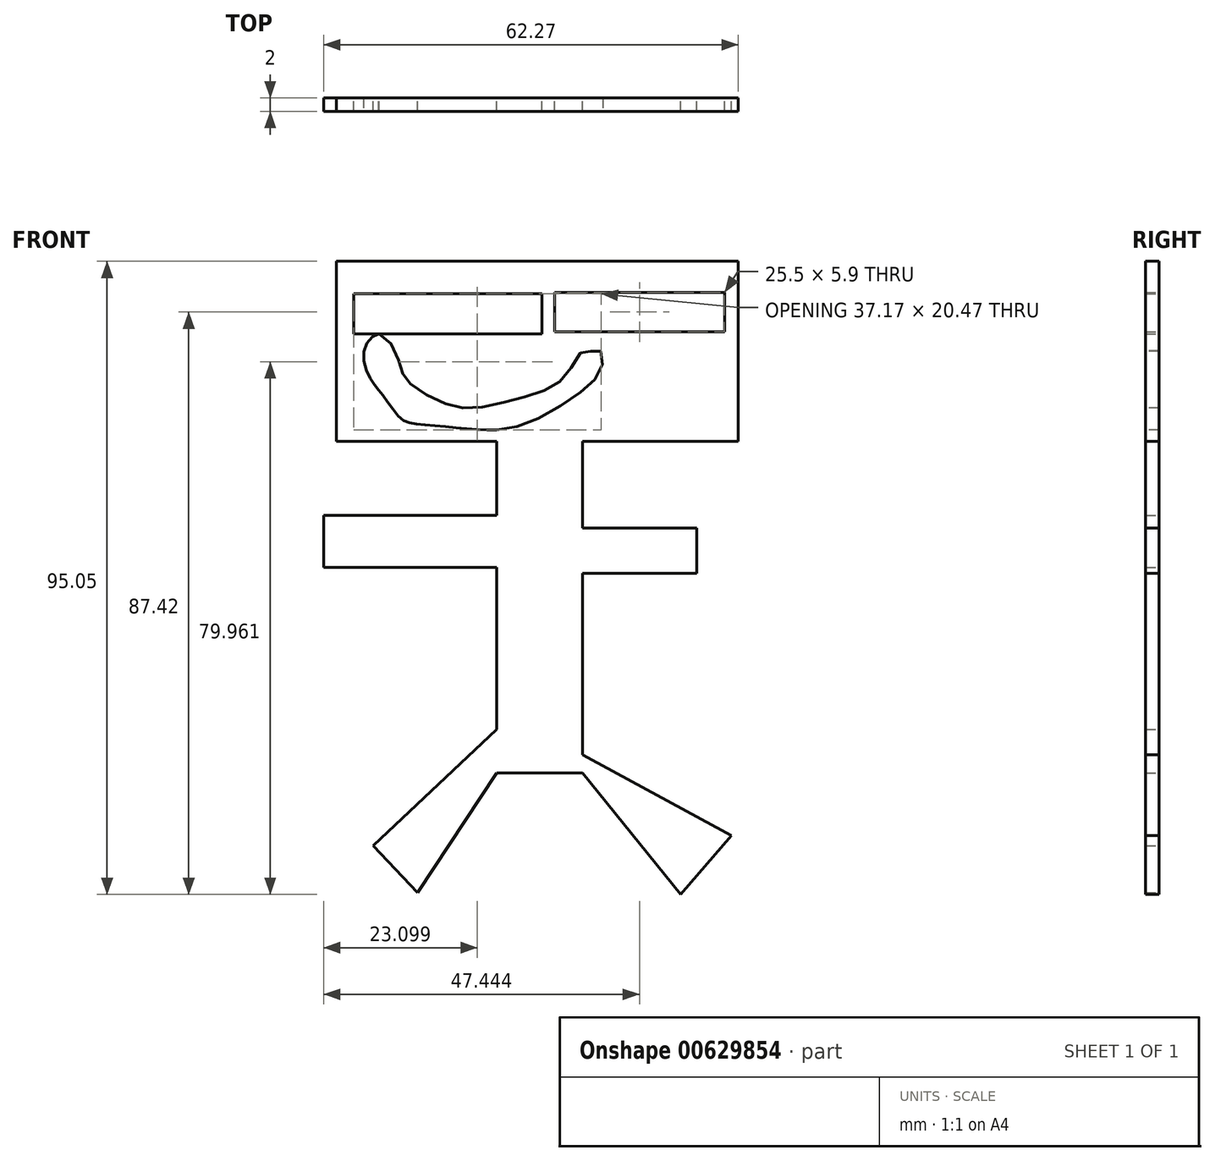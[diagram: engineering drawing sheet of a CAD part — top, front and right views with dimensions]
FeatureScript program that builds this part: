
annotation { "Feature Type Name" : "Feature", "Feature Type Description" : "" }
export const myFeature = defineFeature(function(context is Context, id is Id, definition is map)
    precondition{}
    {
        {
            var Q0;
            Q0=qCreatedBy(makeId("Front.planeOp"),FACE);
            var sketch = newSketch(context, id + "F0", { "sketchPlane" : qUnion([Q0])});
            skLineSegment(sketch, "E0.bottom", {"start": v(-63.66, 35.47) * mm, "end": v(-3.3, 35.47) * mm});
            skLineSegment(sketch, "E0.top", {"start": v(-63.66, 8.41) * mm, "end": v(-3.3, 8.41) * mm});
            skLineSegment(sketch, "E0.left", {"start": v(-63.66, 35.47) * mm, "end": v(-63.66, 8.41) * mm});
            skLineSegment(sketch, "E0.right", {"start": v(-3.3, 35.47) * mm, "end": v(-3.3, 8.41) * mm});
            skLineSegment(sketch, "E1.bottom", {"start": v(-39.55, 10.15) * mm, "end": v(-26.71, 10.15) * mm});
            skLineSegment(sketch, "E1.top", {"start": v(-39.55, -41.37) * mm, "end": v(-26.71, -41.37) * mm});
            skLineSegment(sketch, "E1.left", {"start": v(-39.55, 10.15) * mm, "end": v(-39.55, -41.37) * mm});
            skLineSegment(sketch, "E1.right", {"start": v(-26.71, 10.15) * mm, "end": v(-26.71, -41.37) * mm});
            skLineSegment(sketch, "E2.bottom", {"start": v(-36.25, -10.5) * mm, "end": v(-65.57, -10.5) * mm});
            skLineSegment(sketch, "E2.top", {"start": v(-36.25, -2.69) * mm, "end": v(-65.57, -2.69) * mm});
            skLineSegment(sketch, "E2.left", {"start": v(-36.25, -10.5) * mm, "end": v(-36.25, -2.69) * mm});
            skLineSegment(sketch, "E2.right", {"start": v(-65.57, -10.5) * mm, "end": v(-65.57, -2.69) * mm});
            skLineSegment(sketch, "E3.bottom", {"start": v(-29.14, -11.36) * mm, "end": v(-9.54, -11.36) * mm});
            skLineSegment(sketch, "E3.top", {"start": v(-29.14, -4.6) * mm, "end": v(-9.54, -4.6) * mm});
            skLineSegment(sketch, "E3.left", {"start": v(-29.14, -11.36) * mm, "end": v(-29.14, -4.6) * mm});
            skLineSegment(sketch, "E3.right", {"start": v(-9.54, -11.36) * mm, "end": v(-9.54, -4.6) * mm});
            skLineSegment(sketch, "E4", {"start": v(-39.55, -34.78) * mm, "end": v(-58.1, -52.3) * mm});
            skLineSegment(sketch, "E5", {"start": v(-58.1, -52.3) * mm, "end": v(-51.47, -59.33) * mm});
            skLineSegment(sketch, "E6", {"start": v(-51.47, -59.33) * mm, "end": v(-39.55, -41.37) * mm});
            skLineSegment(sketch, "E7", {"start": v(-26.71, -41.37) * mm, "end": v(-11.97, -59.58) * mm});
            skLineSegment(sketch, "E8", {"start": v(-11.97, -59.58) * mm, "end": v(-4.34, -50.74) * mm});
            skLineSegment(sketch, "E9", {"start": v(-4.34, -50.74) * mm, "end": v(-26.71, -38.6) * mm});
            skLineSegment(sketch, "E10.bottom", {"start": v(-61.06, 30.62) * mm, "end": v(-32.78, 30.62) * mm});
            skLineSegment(sketch, "E10.top", {"start": v(-61.06, 24.54) * mm, "end": v(-32.78, 24.54) * mm});
            skLineSegment(sketch, "E10.left", {"start": v(-61.06, 30.62) * mm, "end": v(-61.06, 24.54) * mm});
            skLineSegment(sketch, "E10.right", {"start": v(-32.78, 30.62) * mm, "end": v(-32.78, 24.54) * mm});
            skLineSegment(sketch, "E11.bottom", {"start": v(-30.88, 24.9) * mm, "end": v(-5.38, 24.9) * mm});
            skLineSegment(sketch, "E11.top", {"start": v(-30.88, 30.79) * mm, "end": v(-5.38, 30.79) * mm});
            skLineSegment(sketch, "E11.left", {"start": v(-30.88, 24.9) * mm, "end": v(-30.88, 30.79) * mm});
            skLineSegment(sketch, "E11.right", {"start": v(-5.38, 24.9) * mm, "end": v(-5.38, 30.79) * mm});
            skPoint(sketch, "E12.0.internal.snap0", {"position": v(-63.66, 21.94) * mm});
            skPoint(sketch, "E12.10.internal.snap0", {"position": v(-63.66, 21.94) * mm});
            skPoint(sketch, "E12.11.internal.snap0", {"position": v(-63.66, 21.94) * mm});
            skPoint(sketch, "E12.12.internal.snap0", {"position": v(-63.66, 21.94) * mm});
            skPoint(sketch, "E12.20.internal.snap0", {"position": v(-63.66, 21.94) * mm});
            skFitSpline(sketch, "E12", {"points": [v(-59.5, 21.94) * mm, v(-58.28, 17.43) * mm, v(-56.55, 15.18) * mm, v(-53.95, 11.88) * mm, v(-51.52, 11.01) * mm, v(-45.62, 10.5) * mm, v(-39.55, 10.15) * mm, v(-33.65, 11.7) * mm, v(-26.71, 16.04) * mm, v(-23.94, 19.17) * mm, v(-23.94, 21.94) * mm, v(-25.15, 21.94) * mm, v(-26.71, 21.94) * mm, v(-28.8, 18.82) * mm, v(-32.09, 16.22) * mm, v(-37.64, 14.48) * mm, v(-43.54, 13.44) * mm, v(-47.87, 14.31) * mm, v(-52.56, 17.09) * mm, v(-53.77, 18.82) * mm, v(-54.81, 21.94) * mm, v(-57.24, 24.54) * mm, v(-59.5, 21.94) * mm]});
            skLineSegment(sketch, "E13.bottom", {"start": v(-62.97, 38.6) * mm, "end": v(24.63, 38.6) * mm});
            skLineSegment(sketch, "E13.top", {"start": v(-62.97, 53.69) * mm, "end": v(24.63, 53.69) * mm});
            skLineSegment(sketch, "E13.left", {"start": v(-62.97, 38.6) * mm, "end": v(-62.97, 53.69) * mm});
            skLineSegment(sketch, "E13.right", {"start": v(24.63, 38.6) * mm, "end": v(24.63, 53.69) * mm});
            skLineSegment(sketch, "E14", {"start": v(-59.84, 40.68) * mm, "end": v(-59.84, 51.78) * mm});
            skLineSegment(sketch, "E15", {"start": v(-59.84, 40.68) * mm, "end": v(-56.37, 40.68) * mm});
            skLineSegment(sketch, "E16", {"start": v(-56.37, 40.68) * mm, "end": v(-56.37, 47.96) * mm});
            skLineSegment(sketch, "E17", {"start": v(-56.37, 47.96) * mm, "end": v(-52.56, 40.68) * mm});
            skLineSegment(sketch, "E18", {"start": v(-52.56, 40.68) * mm, "end": v(-47, 40.68) * mm});
            skLineSegment(sketch, "E19", {"start": v(-47, 40.68) * mm, "end": v(-52.21, 47.96) * mm});
            skLineSegment(sketch, "E20", {"start": v(-59.84, 51.78) * mm, "end": v(-56.37, 51.78) * mm});
            skLineSegment(sketch, "E21", {"start": v(-52.21, 51.78) * mm, "end": v(-56.37, 51.78) * mm});
            skLineSegment(sketch, "E22", {"start": v(-52.21, 51.78) * mm, "end": v(-49.44, 50.39) * mm});
            skLineSegment(sketch, "E23", {"start": v(-49.44, 50.39) * mm, "end": v(-52.21, 47.96) * mm});
            skLineSegment(sketch, "E24", {"start": v(-42.67, 50.39) * mm, "end": v(-42.67, 42.06) * mm});
            skLineSegment(sketch, "E25", {"start": v(-42.67, 42.06) * mm, "end": v(-41.68, 40.68) * mm});
            skLineSegment(sketch, "E26", {"start": v(-41.68, 40.68) * mm, "end": v(-38.68, 40.68) * mm});
            skLineSegment(sketch, "E27", {"start": v(-38.68, 40.68) * mm, "end": v(-36.74, 42.06) * mm});
            skLineSegment(sketch, "E28", {"start": v(-36.74, 42.06) * mm, "end": v(-36.74, 43.97) * mm});
            skLineSegment(sketch, "E29", {"start": v(-36.74, 43.97) * mm, "end": v(-36.74, 50.39) * mm});
            skLineSegment(sketch, "E30", {"start": v(-36.74, 50.39) * mm, "end": v(-38.85, 50.39) * mm});
            skLineSegment(sketch, "E31", {"start": v(-38.85, 50.39) * mm, "end": v(-38.85, 42.06) * mm});
            skLineSegment(sketch, "E32", {"start": v(-38.85, 42.06) * mm, "end": v(-39.83, 41.37) * mm});
            skPoint(sketch, "E32.endSnap0", {"position": v(-42.18, 41.37) * mm});
            skLineSegment(sketch, "E33", {"start": v(-39.83, 41.37) * mm, "end": v(-41.28, 50.39) * mm});
            skLineSegment(sketch, "E34", {"start": v(-41.28, 50.39) * mm, "end": v(-42.67, 50.39) * mm});
            skLineSegment(sketch, "E35", {"start": v(-31.4, 50.39) * mm, "end": v(-31.4, 41.37) * mm});
            skLineSegment(sketch, "E36", {"start": v(-31.4, 41.37) * mm, "end": v(-28.27, 41.37) * mm});
            skLineSegment(sketch, "E37", {"start": v(-28.27, 41.37) * mm, "end": v(-28.27, 46.92) * mm});
            skLineSegment(sketch, "E38", {"start": v(-28.27, 46.92) * mm, "end": v(-25.32, 46.92) * mm});
            skLineSegment(sketch, "E39", {"start": v(-25.32, 46.92) * mm, "end": v(-23.24, 46.92) * mm});
            skLineSegment(sketch, "E40", {"start": v(-23.24, 46.92) * mm, "end": v(-23.24, 49) * mm});
            skLineSegment(sketch, "E41", {"start": v(-23.24, 49) * mm, "end": v(-23.24, 50.39) * mm});
            skLineSegment(sketch, "E42", {"start": v(-23.24, 50.39) * mm, "end": v(-28.27, 52.12) * mm});
            skLineSegment(sketch, "E43", {"start": v(-28.27, 52.12) * mm, "end": v(-31.4, 50.39) * mm});
            skLineSegment(sketch, "E44", {"start": v(-28.27, 49) * mm, "end": v(-28.27, 50.39) * mm});
            skLineSegment(sketch, "E45", {"start": v(-28.27, 50.39) * mm, "end": v(-25.76, 49) * mm});
            skPoint(sketch, "E45.endSnap0", {"position": v(-25.76, 51.26) * mm});
            skLineSegment(sketch, "E46", {"start": v(-25.76, 49) * mm, "end": v(-28.27, 49) * mm});
            skLineSegment(sketch, "E47", {"start": v(-19.17, 46.92) * mm, "end": v(-19.17, 40.68) * mm});
            skPoint(sketch, "E47.startSnap0", {"position": v(-19.17, 53.69) * mm});
            skLineSegment(sketch, "E48", {"start": v(-19.17, 40.68) * mm, "end": v(-13, 40.68) * mm});
            skLineSegment(sketch, "E49", {"start": v(-13, 40.68) * mm, "end": v(-13, 46.92) * mm});
            skLineSegment(sketch, "E50", {"start": v(-13, 46.92) * mm, "end": v(-6.39, 50.39) * mm});
            skLineSegment(sketch, "E51", {"start": v(-6.39, 50.39) * mm, "end": v(-12.49, 50.39) * mm});
            skLineSegment(sketch, "E52", {"start": v(-12.49, 50.39) * mm, "end": v(-15.44, 46.92) * mm});
            skLineSegment(sketch, "E53", {"start": v(-15.44, 46.92) * mm, "end": v(-19.52, 50.39) * mm});
            skLineSegment(sketch, "E54", {"start": v(-19.52, 50.39) * mm, "end": v(-23.24, 50.39) * mm});
            skLineSegment(sketch, "E55", {"start": v(-19.17, 46.92) * mm, "end": v(-23.24, 50.39) * mm});
            skCircle(sketch, "E56", {"center": v(-3.99, 41.02) * mm, "radius": 2.25 * mm});
            skLineSegment(sketch, "E57.bottom", {"start": v(-5.55, 44.84) * mm, "end": v(-2.25, 44.84) * mm});
            skLineSegment(sketch, "E57.top", {"start": v(-5.55, 52.12) * mm, "end": v(-2.25, 52.12) * mm});
            skLineSegment(sketch, "E57.left", {"start": v(-5.55, 44.84) * mm, "end": v(-5.55, 52.12) * mm});
            skLineSegment(sketch, "E57.right", {"start": v(-2.25, 44.84) * mm, "end": v(-2.25, 52.12) * mm});
            skCircle(sketch, "E58", {"center": v(10.4, 45.19) * mm, "radius": 6.45 * mm});
            skCircle(sketch, "E59", {"center": v(7.98, 47.1) * mm, "radius": 1.87 * mm});
            skCircle(sketch, "E60", {"center": v(13, 47.27) * mm, "radius": 1.7 * mm});
            skFitSpline(sketch, "E61", {"points": [v(6.42, 43.8) * mm, v(7.29, 40.68) * mm, v(9.89, 40.68) * mm, v(13, 43.45) * mm, v(11.97, 43.8) * mm, v(10.23, 42.93) * mm, v(8.15, 42.06) * mm, v(6.42, 43.8) * mm]});
            skSolve(sketch);
        }
        {
            var Q0;
            Q0=makeQuery(id+"F0.imprint","IMPRINT",FACE,{"disambiguationData":[TD([[makeQuery(id+"F0.imprint","IMPRINT",EDGE,{"derivedFrom":sQuery(id+"F0.wireOp",EDGE,"E0.bottom")}),-1.0]])]});
            var Q1;
            {var subQ5=sQuery(id+"F0.wireOp",EDGE,"E1.bottom");Q1=makeQuery(id+"F0.imprint","IMPRINT",FACE,{"disambiguationData":[TD([[makeQuery(id+"F0.imprint","IMPRINT",EDGE,{"derivedFrom":subQ5}),-1.0]])]});}
            var Q2;
            {var subQ1=sQuery(id+"F0.wireOp",EDGE,"E1.top");Q2=makeQuery(id+"F0.imprint","IMPRINT",FACE,{"disambiguationData":[TD([[makeQuery(id+"F0.imprint","IMPRINT",EDGE,{"derivedFrom":subQ1}),1.0]])]});}
            var Q3;
            {var subQ5=sQuery(id+"F0.wireOp",EDGE,"E3.left");Q3=makeQuery(id+"F0.imprint","IMPRINT",FACE,{"disambiguationData":[TD([[makeQuery(id+"F0.imprint","IMPRINT",EDGE,{"derivedFrom":subQ5}),-1.0]])]});}
            var Q4;
            {var subQ5=sQuery(id+"F0.wireOp",EDGE,"E2.left");Q4=makeQuery(id+"F0.imprint","IMPRINT",FACE,{"disambiguationData":[TD([[makeQuery(id+"F0.imprint","IMPRINT",EDGE,{"derivedFrom":subQ5}),1.0]])]});}
            var Q5;
            {var subQ5=sQuery(id+"F0.wireOp",EDGE,"E2.right");Q5=makeQuery(id+"F0.imprint","IMPRINT",FACE,{"disambiguationData":[TD([[makeQuery(id+"F0.imprint","IMPRINT",EDGE,{"derivedFrom":subQ5}),-1.0]])]});}
            var Q6;
            {var subQ5=sQuery(id+"F0.wireOp",EDGE,"E3.right");Q6=makeQuery(id+"F0.imprint","IMPRINT",FACE,{"disambiguationData":[TD([[makeQuery(id+"F0.imprint","IMPRINT",EDGE,{"derivedFrom":subQ5}),1.0]])]});}
            var Q7;
            {var subQ2=sQuery(id+"F0.wireOp",EDGE,"E4");Q7=makeQuery(id+"F0.imprint","IMPRINT",FACE,{"disambiguationData":[TD([[makeQuery(id+"F0.imprint","IMPRINT",EDGE,{"derivedFrom":subQ2}),1.0]])]});}
            var Q8;
            {var subQ0=sQuery(id+"F0.wireOp",EDGE,"E7");Q8=makeQuery(id+"F0.imprint","IMPRINT",FACE,{"disambiguationData":[TD([[makeQuery(id+"F0.imprint","IMPRINT",EDGE,{"derivedFrom":subQ0}),1.0]])]});}
            extrude(context, id + "F1", {"entities" : qUnion([Q0, Q1, Q2, Q3, Q4, Q5, Q6, Q7, Q8]), "depth" : 2 * mm, "offsetDistance" : 25 * mm});
        }
    });
